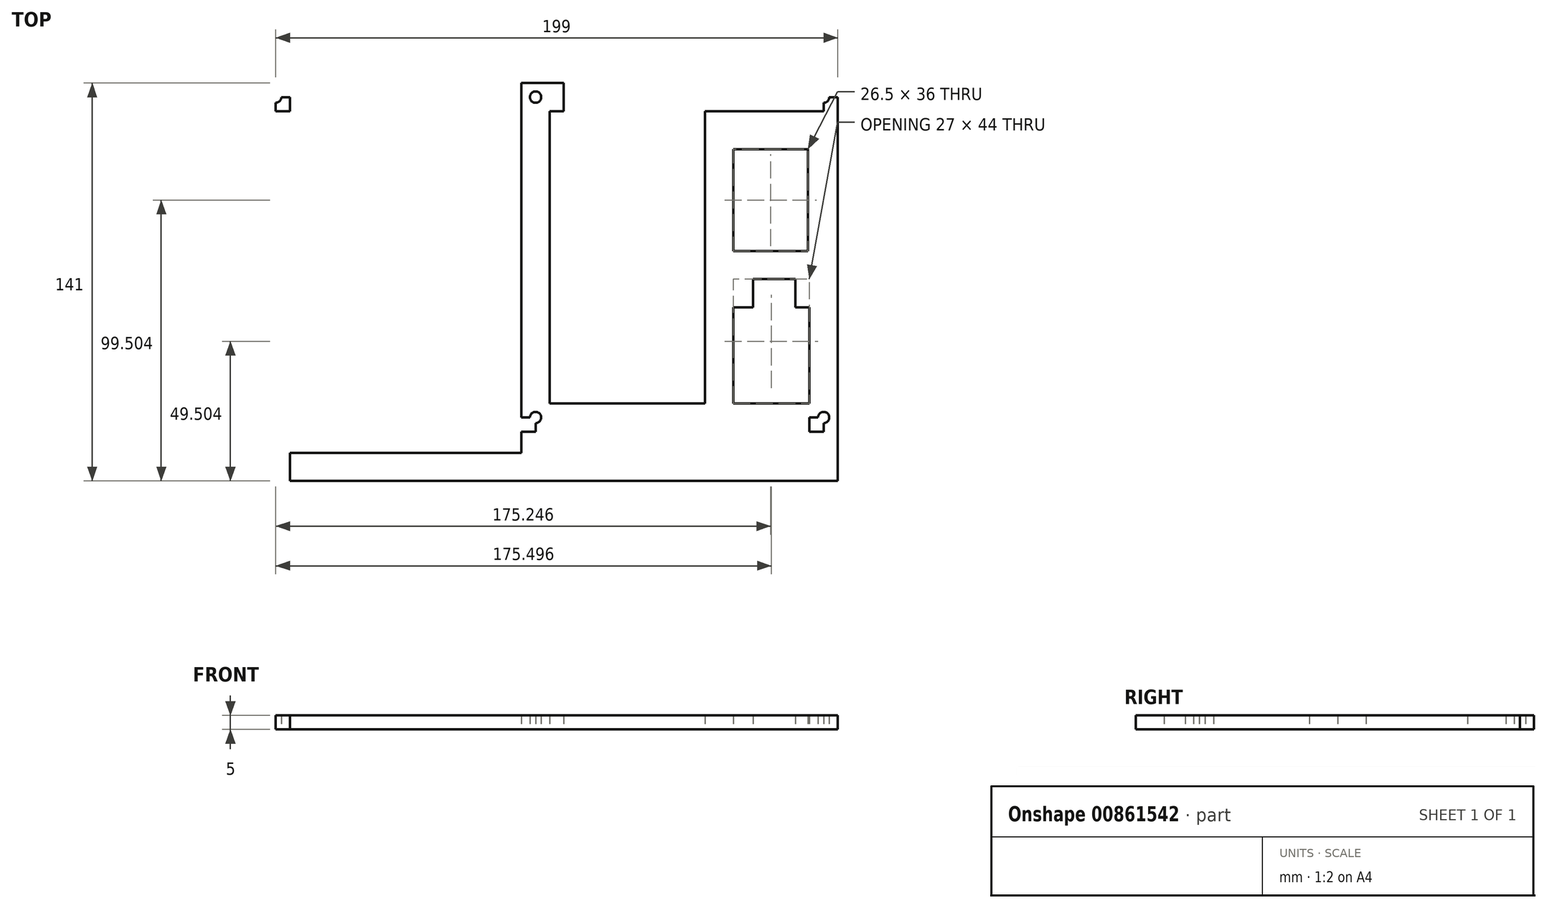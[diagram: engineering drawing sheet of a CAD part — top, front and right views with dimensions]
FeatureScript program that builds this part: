
annotation { "Feature Type Name" : "Feature", "Feature Type Description" : "" }
export const myFeature = defineFeature(function(context is Context, id is Id, definition is map)
    precondition{}
    {
        {
            var Q0;
            Q0=qCreatedBy(makeId("Top.planeOp"),FACE);
            var sketch = newSketch(context, id + "F0", { "sketchPlane" : qUnion([Q0])});
            skLineSegment(sketch, "E0.bottom", {"start": v(-139.34, -1.26) * mm, "end": v(-129.34, -1.26) * mm});
            skLineSegment(sketch, "E0.top", {"start": v(-139.34, -11.26) * mm, "end": v(-129.34, -11.26) * mm});
            skLineSegment(sketch, "E0.left", {"start": v(-139.34, -1.26) * mm, "end": v(-139.34, -11.26) * mm});
            skLineSegment(sketch, "E0.right", {"start": v(-129.34, -1.26) * mm, "end": v(-129.34, -11.26) * mm});
            skLineSegment(sketch, "E1.bottom", {"start": v(-129.34, -11.26) * mm, "end": v(-74.34, -11.26) * mm});
            skLineSegment(sketch, "E1.top", {"start": v(-129.34, -114.76) * mm, "end": v(-74.34, -114.76) * mm});
            skLineSegment(sketch, "E1.left", {"start": v(-129.34, -11.26) * mm, "end": v(-129.34, -114.76) * mm});
            skLineSegment(sketch, "E1.right", {"start": v(-74.34, -11.26) * mm, "end": v(-74.34, -114.76) * mm});
            skLineSegment(sketch, "E2", {"start": v(-74.34, -114.76) * mm, "end": v(-64.34, -114.76) * mm});
            skLineSegment(sketch, "E3.bottom", {"start": v(-64.34, -114.76) * mm, "end": v(-37.34, -114.76) * mm});
            skLineSegment(sketch, "E3.top", {"start": v(-64.34, -80.76) * mm, "end": v(-37.34, -80.76) * mm});
            skLineSegment(sketch, "E3.left", {"start": v(-64.34, -114.76) * mm, "end": v(-64.34, -80.76) * mm});
            skLineSegment(sketch, "E3.right", {"start": v(-37.34, -114.76) * mm, "end": v(-37.34, -80.76) * mm});
            skLineSegment(sketch, "E4", {"start": v(-37.34, -80.76) * mm, "end": v(-42.34, -80.76) * mm});
            skLineSegment(sketch, "E5.bottom", {"start": v(-42.34, -80.76) * mm, "end": v(-57.34, -80.76) * mm});
            skLineSegment(sketch, "E5.top", {"start": v(-42.34, -70.76) * mm, "end": v(-57.34, -70.76) * mm});
            skLineSegment(sketch, "E5.left", {"start": v(-42.34, -80.76) * mm, "end": v(-42.34, -70.76) * mm});
            skLineSegment(sketch, "E5.right", {"start": v(-57.34, -80.76) * mm, "end": v(-57.34, -70.76) * mm});
            skLineSegment(sketch, "E6", {"start": v(-64.34, -80.76) * mm, "end": v(-64.34, -60.76) * mm});
            skLineSegment(sketch, "E7.bottom", {"start": v(-64.34, -60.76) * mm, "end": v(-37.84, -60.76) * mm});
            skLineSegment(sketch, "E7.top", {"start": v(-64.34, -24.76) * mm, "end": v(-37.84, -24.76) * mm});
            skLineSegment(sketch, "E7.left", {"start": v(-64.34, -60.76) * mm, "end": v(-64.34, -24.76) * mm});
            skLineSegment(sketch, "E7.right", {"start": v(-37.84, -60.76) * mm, "end": v(-37.84, -24.76) * mm});
            skLineSegment(sketch, "E8", {"start": v(-74.34, -11.26) * mm, "end": v(-27.34, -11.26) * mm});
            skLineSegment(sketch, "E9.bottom", {"start": v(-129.34, -114.76) * mm, "end": v(-139.34, -114.76) * mm});
            skLineSegment(sketch, "E9.top", {"start": v(-129.34, -124.76) * mm, "end": v(-139.34, -124.76) * mm});
            skLineSegment(sketch, "E9.left", {"start": v(-129.34, -114.76) * mm, "end": v(-129.34, -124.76) * mm});
            skLineSegment(sketch, "E9.right", {"start": v(-139.34, -114.76) * mm, "end": v(-139.34, -124.76) * mm});
            skLineSegment(sketch, "E10.bottom", {"start": v(-37.34, -114.76) * mm, "end": v(-27.34, -114.76) * mm});
            skLineSegment(sketch, "E10.top", {"start": v(-37.34, -124.76) * mm, "end": v(-27.34, -124.76) * mm});
            skLineSegment(sketch, "E10.left", {"start": v(-37.34, -114.76) * mm, "end": v(-37.34, -124.76) * mm});
            skLineSegment(sketch, "E10.right", {"start": v(-27.34, -114.76) * mm, "end": v(-27.34, -124.76) * mm});
            skLineSegment(sketch, "E11.top", {"start": v(-139.34, -124.76) * mm, "end": v(-37.34, -124.76) * mm});
            skLineSegment(sketch, "E12", {"start": v(-129.34, -11.26) * mm, "end": v(-124.34, -11.26) * mm});
            skLineSegment(sketch, "E13", {"start": v(-124.34, -11.26) * mm, "end": v(-124.34, -1.26) * mm});
            skLineSegment(sketch, "E14", {"start": v(-74.34, -11.26) * mm, "end": v(-79.34, -11.26) * mm});
            skLineSegment(sketch, "E15", {"start": v(-79.34, -11.26) * mm, "end": v(-79.34, -1.26) * mm});
            skLineSegment(sketch, "E16.bottom", {"start": v(-129.34, -11.26) * mm, "end": v(-126.54, -11.26) * mm});
            skLineSegment(sketch, "E16.left", {"start": v(-129.34, -11.26) * mm, "end": v(-129.34, -14.06) * mm});
            skLineSegment(sketch, "E17.bottom", {"start": v(-129.34, -114.76) * mm, "end": v(-126.34, -114.76) * mm});
            skLineSegment(sketch, "E17.left", {"start": v(-129.34, -114.76) * mm, "end": v(-129.34, -111.76) * mm});
            skLineSegment(sketch, "E18.bottom", {"start": v(-74.34, -114.76) * mm, "end": v(-77.2, -114.76) * mm});
            skLineSegment(sketch, "E18.left", {"start": v(-74.34, -114.76) * mm, "end": v(-74.34, -111.9) * mm});
            skLineSegment(sketch, "E19.bottom", {"start": v(-74.34, -11.26) * mm, "end": v(-77.34, -11.26) * mm});
            skLineSegment(sketch, "E19.left", {"start": v(-74.34, -11.26) * mm, "end": v(-74.34, -14.26) * mm});
            skLineSegment(sketch, "E20.left", {"start": v(-27.34, -11.26) * mm, "end": v(-27.34, -14.66) * mm});
            skLineSegment(sketch, "E21.bottom", {"start": v(-37.84, -60.76) * mm, "end": v(-39.6, -60.76) * mm});
            skLineSegment(sketch, "E21.left", {"start": v(-37.84, -60.76) * mm, "end": v(-37.84, -59) * mm});
            skLineSegment(sketch, "E22.bottom", {"start": v(-37.84, -24.76) * mm, "end": v(-39.54, -24.76) * mm});
            skLineSegment(sketch, "E22.top", {"start": v(-37.84, -26.46) * mm, "end": v(-39.54, -26.46) * mm});
            skLineSegment(sketch, "E22.left", {"start": v(-37.84, -24.76) * mm, "end": v(-37.84, -26.46) * mm});
            skLineSegment(sketch, "E22.right", {"start": v(-39.54, -24.76) * mm, "end": v(-39.54, -26.46) * mm});
            skLineSegment(sketch, "E23.bottom", {"start": v(-64.34, -24.76) * mm, "end": v(-62.64, -24.76) * mm});
            skLineSegment(sketch, "E23.top", {"start": v(-64.34, -26.46) * mm, "end": v(-62.64, -26.46) * mm});
            skLineSegment(sketch, "E23.left", {"start": v(-64.34, -24.76) * mm, "end": v(-64.34, -26.46) * mm});
            skLineSegment(sketch, "E23.right", {"start": v(-62.64, -24.76) * mm, "end": v(-62.64, -26.46) * mm});
            skLineSegment(sketch, "E24.bottom", {"start": v(-64.34, -60.76) * mm, "end": v(-62.6, -60.76) * mm});
            skLineSegment(sketch, "E24.left", {"start": v(-64.34, -60.76) * mm, "end": v(-64.34, -59) * mm});
            skLineSegment(sketch, "E25.bottom", {"start": v(-64.34, -114.76) * mm, "end": v(-62.4, -114.76) * mm});
            skLineSegment(sketch, "E25.top", {"start": v(-64.34, -105.5) * mm, "end": v(-62.4, -105.5) * mm});
            skLineSegment(sketch, "E25.left", {"start": v(-64.34, -114.76) * mm, "end": v(-64.34, -105.5) * mm});
            skLineSegment(sketch, "E25.right", {"start": v(-62.4, -114.76) * mm, "end": v(-62.4, -105.5) * mm});
            skLineSegment(sketch, "E26.bottom", {"start": v(-37.34, -114.76) * mm, "end": v(-39.3, -114.76) * mm});
            skLineSegment(sketch, "E26.top", {"start": v(-37.34, -105.5) * mm, "end": v(-39.3, -105.5) * mm});
            skLineSegment(sketch, "E26.left", {"start": v(-37.34, -114.76) * mm, "end": v(-37.34, -105.5) * mm});
            skLineSegment(sketch, "E26.right", {"start": v(-39.3, -114.76) * mm, "end": v(-39.3, -105.5) * mm});
            skLineSegment(sketch, "E27.bottom", {"start": v(-37.34, -80.76) * mm, "end": v(-39.3, -80.76) * mm});
            skLineSegment(sketch, "E27.top", {"start": v(-37.34, -82.7) * mm, "end": v(-39.3, -82.7) * mm});
            skLineSegment(sketch, "E27.left", {"start": v(-37.34, -80.76) * mm, "end": v(-37.34, -82.7) * mm});
            skLineSegment(sketch, "E27.right", {"start": v(-39.3, -80.76) * mm, "end": v(-39.3, -82.7) * mm});
            skLineSegment(sketch, "E28.bottom", {"start": v(-64.34, -80.76) * mm, "end": v(-62.4, -80.76) * mm});
            skLineSegment(sketch, "E28.top", {"start": v(-64.34, -82.7) * mm, "end": v(-62.4, -82.7) * mm});
            skLineSegment(sketch, "E28.left", {"start": v(-64.34, -80.76) * mm, "end": v(-64.34, -82.7) * mm});
            skLineSegment(sketch, "E28.right", {"start": v(-62.4, -80.76) * mm, "end": v(-62.4, -82.7) * mm});
            skCircle(sketch, "E29", {"center": v(-39.3, -105.5) * mm, "radius": 1.15 * mm});
            skCircle(sketch, "E30", {"center": v(-62.4, -105.5) * mm, "radius": 1.15 * mm});
            skCircle(sketch, "E31", {"center": v(-62.4, -82.7) * mm, "radius": 1.15 * mm});
            skCircle(sketch, "E32", {"center": v(-39.3, -82.7) * mm, "radius": 1.15 * mm});
            skCircle(sketch, "E33", {"center": v(-62.64, -26.46) * mm, "radius": 1.2 * mm});
            skCircle(sketch, "E34", {"center": v(-39.54, -26.46) * mm, "radius": 1.2 * mm});
            skLineSegment(sketch, "E35.top", {"start": v(-37.34, -124.76) * mm, "end": v(-139.34, -124.76) * mm});
            skLineSegment(sketch, "E36.bottom", {"start": v(-139.34, -124.76) * mm, "end": v(-134.34, -124.76) * mm});
            skLineSegment(sketch, "E36.top", {"start": v(-139.34, -119.76) * mm, "end": v(-134.34, -119.76) * mm});
            skLineSegment(sketch, "E36.left", {"start": v(-139.34, -124.76) * mm, "end": v(-139.34, -119.76) * mm});
            skLineSegment(sketch, "E36.right", {"start": v(-134.34, -124.76) * mm, "end": v(-134.34, -119.76) * mm});
            skCircle(sketch, "E37", {"center": v(-134.34, -119.76) * mm, "radius": 2 * mm});
            skLineSegment(sketch, "E38.bottom", {"start": v(-37.34, -124.76) * mm, "end": v(-32.34, -124.76) * mm});
            skLineSegment(sketch, "E38.top", {"start": v(-37.34, -119.76) * mm, "end": v(-32.34, -119.76) * mm});
            skLineSegment(sketch, "E38.left", {"start": v(-37.34, -124.76) * mm, "end": v(-37.34, -119.76) * mm});
            skLineSegment(sketch, "E38.right", {"start": v(-32.34, -124.76) * mm, "end": v(-32.34, -119.76) * mm});
            skCircle(sketch, "E39", {"center": v(-32.34, -119.76) * mm, "radius": 2 * mm});
            skLineSegment(sketch, "E40.bottom", {"start": v(-139.34, -1.26) * mm, "end": v(-134.34, -1.26) * mm});
            skLineSegment(sketch, "E40.top", {"start": v(-139.34, -6.26) * mm, "end": v(-134.34, -6.26) * mm});
            skLineSegment(sketch, "E40.left", {"start": v(-139.34, -1.26) * mm, "end": v(-139.34, -6.26) * mm});
            skLineSegment(sketch, "E40.right", {"start": v(-134.34, -1.26) * mm, "end": v(-134.34, -6.26) * mm});
            skCircle(sketch, "E41", {"center": v(-134.34, -6.26) * mm, "radius": 2 * mm});
            skLineSegment(sketch, "E42.bottom", {"start": v(-129.34, -11.26) * mm, "end": v(-126.34, -11.26) * mm});
            skLineSegment(sketch, "E42.left", {"start": v(-129.34, -11.26) * mm, "end": v(-129.34, -27.96) * mm});
            skLineSegment(sketch, "E43.top", {"start": v(-129.34, -108.76) * mm, "end": v(-126.34, -108.76) * mm});
            skLineSegment(sketch, "E43.left", {"start": v(-129.34, -114.76) * mm, "end": v(-129.34, -108.76) * mm});
            skLineSegment(sketch, "E43.right", {"start": v(-126.34, -114.76) * mm, "end": v(-126.34, -108.76) * mm});
            skLineSegment(sketch, "E44.bottom", {"start": v(-74.34, -114.76) * mm, "end": v(-77.34, -114.76) * mm});
            skLineSegment(sketch, "E44.top", {"start": v(-74.34, -103.16) * mm, "end": v(-77.34, -103.16) * mm});
            skLineSegment(sketch, "E44.left", {"start": v(-74.34, -114.76) * mm, "end": v(-74.34, -103.16) * mm});
            skLineSegment(sketch, "E44.right", {"start": v(-77.34, -114.76) * mm, "end": v(-77.34, -103.16) * mm});
            skLineSegment(sketch, "E45.top", {"start": v(-74.34, -26.06) * mm, "end": v(-77.34, -26.06) * mm});
            skLineSegment(sketch, "E45.left", {"start": v(-74.34, -114.76) * mm, "end": v(-74.34, -26.06) * mm});
            skLineSegment(sketch, "E45.right", {"start": v(-77.34, -114.76) * mm, "end": v(-77.34, -26.06) * mm});
            skLineSegment(sketch, "E46.top", {"start": v(-129.34, -27.46) * mm, "end": v(-126.34, -27.46) * mm});
            skLineSegment(sketch, "E46.left", {"start": v(-129.34, -114.76) * mm, "end": v(-129.34, -27.46) * mm});
            skLineSegment(sketch, "E46.right", {"start": v(-126.34, -114.76) * mm, "end": v(-126.34, -27.46) * mm});
            skCircle(sketch, "E47", {"center": v(-126.34, -108.76) * mm, "radius": 2 * mm});
            skCircle(sketch, "E48", {"center": v(-126.34, -27.46) * mm, "radius": 2 * mm});
            skCircle(sketch, "E49", {"center": v(-77.34, -26.06) * mm, "radius": 2 * mm});
            skCircle(sketch, "E50", {"center": v(-77.34, -103.16) * mm, "radius": 2 * mm});
            skLineSegment(sketch, "E51", {"start": v(-139.34, -1.26) * mm, "end": v(-83.34, -1.26) * mm});
            skLineSegment(sketch, "E52.bottom", {"start": v(-83.34, -1.26) * mm, "end": v(-139.34, -1.26) * mm});
            skLineSegment(sketch, "E53.MirrorCS", {"start": v(-139.5, -132.26) * mm, "end": v(-139.5, -11.26) * mm});
            skLineSegment(sketch, "E54.MirrorCS", {"start": v(-221.34, -11.26) * mm, "end": v(-139.34, -11.26) * mm});
            skLineSegment(sketch, "E55.MirrorCS", {"start": v(-221.34, -132.26) * mm, "end": v(-139.34, -132.26) * mm});
            skCircle(sketch, "E56.MirrorC", {"center": v(-142.74, -128.86) * mm, "radius": 1.4 * mm});
            skCircle(sketch, "E57.MirrorC", {"center": v(-217.94, -128.86) * mm, "radius": 1.7 * mm});
            skCircle(sketch, "E58.MirrorC", {"center": v(-217.94, -14.66) * mm, "radius": 1.4 * mm});
            skCircle(sketch, "E59.MirrorC", {"center": v(-142.74, -14.66) * mm, "radius": 1.4 * mm});
            skLineSegment(sketch, "E60.MirrorCS", {"start": v(-142.74, -11.26) * mm, "end": v(-142.74, -14.66) * mm});
            skLineSegment(sketch, "E61.MirrorCS", {"start": v(-139.34, -14.66) * mm, "end": v(-142.74, -14.66) * mm});
            skLineSegment(sketch, "E62.MirrorCS", {"start": v(-217.94, -11.26) * mm, "end": v(-217.94, -14.66) * mm});
            skLineSegment(sketch, "E63.MirrorCS", {"start": v(-221.34, -14.66) * mm, "end": v(-217.94, -14.66) * mm});
            skLineSegment(sketch, "E64.MirrorCS", {"start": v(-142.74, -132.26) * mm, "end": v(-142.74, -128.86) * mm});
            skLineSegment(sketch, "E65.MirrorCS", {"start": v(-139.34, -128.86) * mm, "end": v(-142.74, -128.86) * mm});
            skLineSegment(sketch, "E66.MirrorCS", {"start": v(-221.34, -128.86) * mm, "end": v(-217.94, -128.86) * mm});
            skLineSegment(sketch, "E67.MirrorCS", {"start": v(-217.94, -132.26) * mm, "end": v(-217.94, -128.86) * mm});
            skLineSegment(sketch, "E68.MirrorCS", {"start": v(-27.34, -1.26) * mm, "end": v(-231.34, -1.26) * mm});
            skLineSegment(sketch, "E69", {"start": v(-221.34, -11.26) * mm, "end": v(-221.34, -1.26) * mm});
            skLineSegment(sketch, "E70", {"start": v(-221.34, -132.26) * mm, "end": v(-221.34, -11.26) * mm});
            skLineSegment(sketch, "E71", {"start": v(-221.34, -132.26) * mm, "end": v(-231.5, -132.26) * mm});
            skLineSegment(sketch, "E72", {"start": v(-27.34, -11.26) * mm, "end": v(-27.34, -1.26) * mm});
            skLineSegment(sketch, "E73.bottom", {"start": v(-221.34, -132.26) * mm, "end": v(-231.34, -132.26) * mm});
            skLineSegment(sketch, "E73.top", {"start": v(-221.34, -142.26) * mm, "end": v(-231.34, -142.26) * mm});
            skLineSegment(sketch, "E73.left", {"start": v(-221.34, -132.26) * mm, "end": v(-221.34, -142.26) * mm});
            skLineSegment(sketch, "E73.right", {"start": v(-231.34, -132.26) * mm, "end": v(-231.34, -142.26) * mm});
            skLineSegment(sketch, "E74.bottom", {"start": v(-221.34, -142.26) * mm, "end": v(-139.34, -142.26) * mm});
            skLineSegment(sketch, "E74.left", {"start": v(-221.34, -142.26) * mm, "end": v(-221.34, -132.26) * mm});
            skLineSegment(sketch, "E75", {"start": v(-27.34, -114.76) * mm, "end": v(-27.34, -11.26) * mm});
            skLineSegment(sketch, "E76", {"start": v(-231.34, -132.26) * mm, "end": v(-231.34, -1.26) * mm});
            skLineSegment(sketch, "E77.bottom", {"start": v(-129.34, -124.76) * mm, "end": v(-139.2, -124.76) * mm});
            skLineSegment(sketch, "E77.top", {"start": v(-129.34, -142.26) * mm, "end": v(-139.34, -142.26) * mm});
            skLineSegment(sketch, "E77.left", {"start": v(-129.34, -124.76) * mm, "end": v(-129.34, -142.26) * mm});
            skLineSegment(sketch, "E78", {"start": v(-139.34, -142.26) * mm, "end": v(-139.5, -132.26) * mm});
            skLineSegment(sketch, "E79.bottom", {"start": v(-231.34, -142.26) * mm, "end": v(-226.34, -142.26) * mm});
            skLineSegment(sketch, "E79.top", {"start": v(-231.34, -137.4) * mm, "end": v(-226.34, -137.4) * mm});
            skLineSegment(sketch, "E79.left", {"start": v(-231.34, -142.26) * mm, "end": v(-231.34, -137.4) * mm});
            skLineSegment(sketch, "E79.right", {"start": v(-226.34, -142.26) * mm, "end": v(-226.34, -137.4) * mm});
            skCircle(sketch, "E80", {"center": v(-226.34, -137.4) * mm, "radius": 2 * mm});
            skLineSegment(sketch, "E81.bottom", {"start": v(-221.34, -11.26) * mm, "end": v(-226.34, -11.26) * mm});
            skLineSegment(sketch, "E81.top", {"start": v(-221.34, -6.26) * mm, "end": v(-226.34, -6.26) * mm});
            skLineSegment(sketch, "E81.left", {"start": v(-221.34, -11.26) * mm, "end": v(-221.34, -6.26) * mm});
            skLineSegment(sketch, "E81.right", {"start": v(-226.34, -11.26) * mm, "end": v(-226.34, -6.26) * mm});
            skCircle(sketch, "E82", {"center": v(-226.34, -6.26) * mm, "radius": 2 * mm});
            skLineSegment(sketch, "E83.bottom", {"start": v(-27.34, -11.26) * mm, "end": v(-32.34, -11.26) * mm});
            skLineSegment(sketch, "E83.top", {"start": v(-27.34, -6.26) * mm, "end": v(-32.34, -6.26) * mm});
            skLineSegment(sketch, "E83.left", {"start": v(-27.34, -11.26) * mm, "end": v(-27.34, -6.26) * mm});
            skLineSegment(sketch, "E83.right", {"start": v(-32.34, -11.26) * mm, "end": v(-32.34, -6.26) * mm});
            skCircle(sketch, "E84", {"center": v(-32.34, -6.26) * mm, "radius": 2 * mm});
            skLineSegment(sketch, "E85.bottom", {"start": v(-129.34, -142.26) * mm, "end": v(-77.34, -142.26) * mm});
            skLineSegment(sketch, "E85.top", {"start": v(-129.34, -114.76) * mm, "end": v(-77.34, -114.76) * mm});
            skLineSegment(sketch, "E85.left", {"start": v(-129.34, -142.26) * mm, "end": v(-129.34, -114.76) * mm});
            skLineSegment(sketch, "E86.bottom", {"start": v(-129.34, -142.26) * mm, "end": v(-74.34, -142.26) * mm});
            skLineSegment(sketch, "E86.right", {"start": v(-74.34, -142.26) * mm, "end": v(-74.34, -114.76) * mm});
            skLineSegment(sketch, "E87", {"start": v(-37.84, -24.76) * mm, "end": v(-27.34, -24.76) * mm});
            skLineSegment(sketch, "E88.bottom", {"start": v(-74.34, -142.26) * mm, "end": v(-27.34, -142.26) * mm});
            skLineSegment(sketch, "E88.top", {"start": v(-74.34, -124.76) * mm, "end": v(-27.34, -124.76) * mm});
            skLineSegment(sketch, "E88.left", {"start": v(-74.34, -142.26) * mm, "end": v(-74.34, -124.76) * mm});
            skLineSegment(sketch, "E88.right", {"start": v(-27.34, -142.26) * mm, "end": v(-27.34, -124.76) * mm});
            skLineSegment(sketch, "E89.bottom", {"start": v(-139.34, -132.26) * mm, "end": v(-151.42, -132.26) * mm});
            skLineSegment(sketch, "E89.top", {"start": v(-139.34, -11.26) * mm, "end": v(-151.42, -11.26) * mm});
            skLineSegment(sketch, "E89.left", {"start": v(-139.34, -132.26) * mm, "end": v(-139.34, -11.26) * mm});
            skLineSegment(sketch, "E89.right", {"start": v(-151.42, -132.26) * mm, "end": v(-151.42, -11.26) * mm});
            skLineSegment(sketch, "E90.bottom", {"start": v(-151.42, -132.26) * mm, "end": v(-147.42, -132.26) * mm});
            skLineSegment(sketch, "E90.top", {"start": v(-151.42, -11.26) * mm, "end": v(-147.42, -11.26) * mm});
            skLineSegment(sketch, "E90.right", {"start": v(-147.42, -132.26) * mm, "end": v(-147.42, -11.26) * mm});
            skLineSegment(sketch, "E91.top", {"start": v(-151.42, -127.18) * mm, "end": v(-147.42, -127.18) * mm});
            skLineSegment(sketch, "E91.left", {"start": v(-151.42, -132.26) * mm, "end": v(-151.42, -127.18) * mm});
            skLineSegment(sketch, "E91.right", {"start": v(-147.42, -132.26) * mm, "end": v(-147.42, -127.18) * mm});
            skLineSegment(sketch, "E92.top", {"start": v(-151.42, -86.54) * mm, "end": v(-147.42, -86.54) * mm});
            skLineSegment(sketch, "E92.left", {"start": v(-151.42, -127.18) * mm, "end": v(-151.42, -86.54) * mm});
            skLineSegment(sketch, "E92.right", {"start": v(-147.42, -127.18) * mm, "end": v(-147.42, -86.54) * mm});
            skSolve(sketch);
        }
        {
            var Q0;
            Q0=makeQuery(id+"F0.imprint","IMPRINT",FACE,{"disambiguationData":[TD([[makeQuery(id+"F0.imprint","IMPRINT",EDGE,{"derivedFrom":sQuery(id+"F0.wireOp",EDGE,"E1.right")}),1.0]])]});
            var Q1;
            Q1=makeQuery(id+"F0.imprint","IMPRINT",FACE,{"disambiguationData":[TD([[makeQuery(id+"F0.imprint","IMPRINT",EDGE,{"derivedFrom":sQuery(id+"F0.wireOp",EDGE,"E10.bottom")}),-1.0]])]});
            var Q2;
            Q2=makeQuery(id+"F0.imprint","IMPRINT",FACE,{"disambiguationData":[TD([[makeQuery(id+"F0.imprint","IMPRINT",EDGE,{"derivedFrom":sQuery(id+"F0.wireOp",EDGE,"E1.top")}),-1.0]])]});
            var Q3;
            Q3=makeQuery(id+"F0.imprint","IMPRINT",FACE,{"disambiguationData":[TD([[makeQuery(id+"F0.imprint","IMPRINT",EDGE,{"derivedFrom":sQuery(id+"F0.wireOp",EDGE,"E9.bottom")}),1.0]])]});
            var Q4;
            Q4=makeQuery(id+"F0.imprint","IMPRINT",FACE,{"disambiguationData":[TD([[makeQuery(id+"F0.imprint","IMPRINT",EDGE,{"derivedFrom":sQuery(id+"F0.wireOp",EDGE,"97myMdQA-agTY-EE5a-eSU0-3Ky6piHqa90I.left")}),1.0]])]});
            var Q5;
            Q5=makeQuery(id+"F0.imprint","IMPRINT",FACE,{"disambiguationData":[TD([[makeQuery(id+"F0.imprint","IMPRINT",EDGE,{"derivedFrom":sQuery(id+"F0.wireOp",EDGE,"E0.bottom")}),-1.0]])]});
            var Q6;
            {var subQ0=sQuery(id+"F0.wireOp",EDGE,"E0.right");Q6=makeQuery(id+"F0.imprint","IMPRINT",FACE,{"disambiguationData":[TD([[makeQuery(id+"F0.imprint","IMPRINT",EDGE,{"derivedFrom":subQ0}),1.0]])]});}
            var Q7;
            {var subQ2=sQuery(id+"F0.wireOp",EDGE,"97myMdQA-agTY-EE5a-eSU0-3Ky6piHqa90I.right");Q7=makeQuery(id+"F0.imprint","IMPRINT",FACE,{"disambiguationData":[TD([[makeQuery(id+"F0.imprint","IMPRINT",EDGE,{"derivedFrom":subQ2}),-1.0]])]});}
            var Q8;
            {var subQ0=sQuery(id+"F0.wireOp",EDGE,"E10.top");Q8=makeQuery(id+"F0.imprint","IMPRINT",FACE,{"disambiguationData":[TD([[makeQuery(id+"F0.imprint","IMPRINT",EDGE,{"derivedFrom":subQ0}),-1.0]])]});}
            var Q9;
            {var subQ1=sQuery(id+"F0.wireOp",EDGE,"R2WY0SRa-AH7d-UwmP-SjNj-uamWJIKeu4LY.bottom");Q9=makeQuery(id+"F0.imprint","IMPRINT",FACE,{"disambiguationData":[TD([[makeQuery(id+"F0.imprint","IMPRINT",EDGE,{"derivedFrom":subQ1}),1.0]])]});}
            var Q10;
            {var subQ1=sQuery(id+"F0.wireOp",EDGE,"E36.bottom");Q10=makeQuery(id+"F0.imprint","IMPRINT",FACE,{"disambiguationData":[TD([[makeQuery(id+"F0.imprint","IMPRINT",EDGE,{"derivedFrom":subQ1}),1.0]])]});}
            var Q11;
            {var subQ1=sQuery(id+"F0.wireOp",EDGE,"E40.bottom");Q11=makeQuery(id+"F0.imprint","IMPRINT",FACE,{"disambiguationData":[TD([[makeQuery(id+"F0.imprint","IMPRINT",EDGE,{"derivedFrom":subQ1}),-1.0]])]});}
            var Q12;
            {var subQ1=sQuery(id+"F0.wireOp",EDGE,"E38.bottom");Q12=makeQuery(id+"F0.imprint","IMPRINT",FACE,{"disambiguationData":[TD([[makeQuery(id+"F0.imprint","IMPRINT",EDGE,{"derivedFrom":subQ1}),1.0]])]});}
            var Q13;
            {var subQ1=sQuery(id+"F0.wireOp",EDGE,"E77.top");Q13=makeQuery(id+"F0.imprint","IMPRINT",FACE,{"disambiguationData":[TD([[makeQuery(id+"F0.imprint","IMPRINT",EDGE,{"derivedFrom":subQ1}),-1.0]])]});}
            var Q14;
            Q14=makeQuery(id+"F0.imprint","IMPRINT",FACE,{"disambiguationData":[TD([[makeQuery(id+"F0.imprint","IMPRINT",EDGE,{"derivedFrom":sQuery(id+"F0.wireOp",EDGE,"E73.bottom")}),1.0]])]});
            var Q15;
            {var subQ4=sQuery(id+"F0.wireOp",EDGE,"E69");Q15=makeQuery(id+"F0.imprint","IMPRINT",FACE,{"disambiguationData":[TD([[makeQuery(id+"F0.imprint","IMPRINT",EDGE,{"derivedFrom":subQ4}),1.0]])]});}
            var Q16;
            {var subQ12=sQuery(id+"F0.wireOp",EDGE,"E0.top");Q16=makeQuery(id+"F0.imprint","IMPRINT",FACE,{"disambiguationData":[TD([[makeQuery(id+"F0.imprint","IMPRINT",EDGE,{"derivedFrom":subQ12}),-1.0]])]});}
            var Q17;
            {var subQ5=sQuery(id+"F0.wireOp",EDGE,"E0.top");Q17=makeQuery(id+"F0.imprint","IMPRINT",FACE,{"disambiguationData":[TD([[makeQuery(id+"F0.imprint","IMPRINT",EDGE,{"derivedFrom":subQ5}),1.0]])]});}
            var Q18;
            Q18=makeQuery(id+"F0.imprint","IMPRINT",FACE,{"disambiguationData":[TD([[makeQuery(id+"F0.imprint","IMPRINT",EDGE,{"derivedFrom":sQuery(id+"F0.wireOp",EDGE,"E8")}),1.0]])]});
            var Q19;
            {var subQ5=sQuery(id+"F0.wireOp",EDGE,"E40.left");Q19=makeQuery(id+"F0.imprint","IMPRINT",FACE,{"disambiguationData":[TD([[makeQuery(id+"F0.imprint","IMPRINT",EDGE,{"derivedFrom":subQ5}),1.0]])]});}
            var Q20;
            {var subQ1=sQuery(id+"F0.wireOp",EDGE,"E79.bottom");Q20=makeQuery(id+"F0.imprint","IMPRINT",FACE,{"disambiguationData":[TD([[makeQuery(id+"F0.imprint","IMPRINT",EDGE,{"derivedFrom":subQ1}),1.0]])]});}
            var Q21;
            {var subQ1=sQuery(id+"F0.wireOp",EDGE,"E83.bottom");Q21=makeQuery(id+"F0.imprint","IMPRINT",FACE,{"disambiguationData":[TD([[makeQuery(id+"F0.imprint","IMPRINT",EDGE,{"derivedFrom":subQ1}),-1.0]])]});}
            var Q22;
            {var subQ1=sQuery(id+"F0.wireOp",EDGE,"E81.bottom");Q22=makeQuery(id+"F0.imprint","IMPRINT",FACE,{"disambiguationData":[TD([[makeQuery(id+"F0.imprint","IMPRINT",EDGE,{"derivedFrom":subQ1}),-1.0]])]});}
            var Q23;
            Q23=makeQuery(id+"F0.imprint","IMPRINT",FACE,{"disambiguationData":[TD([[makeQuery(id+"F0.imprint","IMPRINT",EDGE,{"derivedFrom":sQuery(id+"F0.wireOp",EDGE,"E74.bottom")}),1.0]])]});
            var Q24;
            {var subQ5=sQuery(id+"F0.wireOp",EDGE,"E85.bottom");Q24=makeQuery(id+"F0.imprint","IMPRINT",FACE,{"disambiguationData":[TD([[makeQuery(id+"F0.imprint","IMPRINT",EDGE,{"derivedFrom":subQ5}),1.0]])]});}
            var Q25;
            {var subQ0=sQuery(id+"F0.wireOp",EDGE,"E85.right");var subQ6=sQuery(id+"F0.wireOp",EDGE,"E35.top");var subQ8=makeQuery(id+"F0.imprint","INTERSECT",VERTEX,{"derivedFrom":[subQ6,subQ0]});Q25=makeQuery(id+"F0.imprint","IMPRINT",FACE,{"disambiguationData":[TD([[makeQuery(id+"F0.imprint","IMPRINT",EDGE,{"disambiguationData":[TD([[subQ8,-1.0]])],"derivedFrom":subQ6}),-1.0]])]});}
            var Q26;
            {var subQ5=sQuery(id+"F0.wireOp",EDGE,"E2");Q26=makeQuery(id+"F0.imprint","IMPRINT",FACE,{"disambiguationData":[TD([[makeQuery(id+"F0.imprint","IMPRINT",EDGE,{"derivedFrom":subQ5}),-1.0]])]});}
            var Q27;
            {var subQ3=sQuery(id+"F0.wireOp",EDGE,"E86.right");var subQ5=sQuery(id+"F0.wireOp",EDGE,"E86.bottom");var subQ7=makeQuery(id+"F0.imprint","INTERSECT",VERTEX,{"derivedFrom":[subQ5,subQ3]});Q27=makeQuery(id+"F0.imprint","IMPRINT",FACE,{"disambiguationData":[TD([[makeQuery(id+"F0.imprint","IMPRINT",EDGE,{"disambiguationData":[TD([[subQ7,-1.0]])],"derivedFrom":subQ3}),1.0]])]});}
            var Q28;
            Q28=makeQuery(id+"F0.imprint","IMPRINT",FACE,{"disambiguationData":[TD([[makeQuery(id+"F0.imprint","IMPRINT",EDGE,{"derivedFrom":sQuery(id+"F0.wireOp",EDGE,"E3.top")}),1.0]])]});
            var Q29;
            {var subQ5=sQuery(id+"F0.wireOp",EDGE,"E38.left");Q29=makeQuery(id+"F0.imprint","IMPRINT",FACE,{"disambiguationData":[TD([[makeQuery(id+"F0.imprint","IMPRINT",EDGE,{"derivedFrom":subQ5}),-1.0]])]});}
            var Q30;
            {var subQ0=sQuery(id+"F0.wireOp",EDGE,"E35.top");Q30=makeQuery(id+"F0.imprint","IMPRINT",FACE,{"disambiguationData":[TD([[makeQuery(id+"F0.imprint","IMPRINT",EDGE,{"derivedFrom":subQ0}),1.0]])]});}
            var Q31;
            Q31=makeQuery(id+"F0.imprint","IMPRINT",FACE,{"disambiguationData":[TD([[makeQuery(id+"F0.imprint","IMPRINT",EDGE,{"derivedFrom":sQuery(id+"F0.wireOp",EDGE,"E88.bottom")}),1.0]])]});
            extrude(context, id + "F1", {"entities" : qUnion([Q0, Q1, Q2, Q3, Q4, Q5, Q6, Q7, Q8, Q9, Q10, Q11, Q12, Q13, Q14, Q15, Q16, Q17, Q18, Q19, Q20, Q21, Q22, Q23, Q24, Q25, Q26, Q27, Q28, Q29, Q30, Q31]), "depth" : 5 * mm, "offsetDistance" : 25 * mm});
        }
    });
